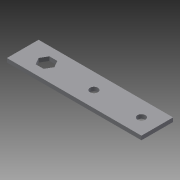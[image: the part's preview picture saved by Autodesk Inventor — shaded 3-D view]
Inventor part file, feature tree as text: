
AUTODESK INVENTOR PART (.ipt)
format: ipt  version: 2013 (Build 170138000, 138)  size: 125,440 bytes
history: native  units: in
note: dims shown in document units (in); Inventor stores cm internally (conversion verified against a paired STEP export)
features: extrude x6, sketch x6
ambient origin geometry x8: Origin, YZ Plane, XZ Plane, XY Plane, X Axis, Y Axis, Z Axis, Center Point
bodies: Solid1 (feature_tree)
feature tree (12):
  extrude  "Extrusion1"  Depth=1.0in
  extrude  "Extrusion2"  Depth=0.5in
  extrude  "Extrusion3"  Depth=1.5in
  extrude  "Extrusion4"  TaperAngle=0.0deg  [1 undecoded]
  extrude  "Extrusion5"  Depth=0.25in
  extrude  "Extrusion6"  Depth=1.5in
  sketch  "Sketch1"  dims[d0=4.0in d1=1.0in]
  sketch  "Sketch2"  dims[d2=0.125in d3=0.0in d4=0.5in]
  sketch  "Sketch3"  dims[d5=0.125in d6=0.0in d7=1.5in]
  sketch  "Sketch4"  dims[d8=3.0in d9=0.0in]
  sketch  "Sketch5"  dims[d10=0.25in d11=0.25in]
  sketch  "Sketch6"  dims[d12=0.125in d13=0.0in d14=1.5in d15=1.0in d16=1.0in d17=0.0in d18=1.5in d19=0.0in d20=0.25in d21=1.5in d22=1.0in d23=0.125in d24=0.0in d25=0.25in d26=0.0in]
note: 1 required parameter value undecoded (feature->parameter linkage not recoverable at this tier; creation-order binding heuristic only, values carry confidence <= 0.55)
